# Revit family: 45-56-001-DN50-400
name_source: partatom
category: Pipe Accessories
units: mm (PartAtom-declared; Revit-internal decimal feet)

## family parameters
Always vertical = No
Cut with Voids When Loaded = No
Part Type = Valve - Breaks Into
Round Connector Dimension = Use Diameter
Shared = No
Work Plane-Based = No

## types (11) — shared parameters
Body_Wallthickness = 15 mm  [stored 0.0492126 ft]
DN 050 = Yes
DN 065 = Yes
DN 080 = Yes
DN 100 = Yes
DN 150 = Yes
DN 200 = Yes
DN 250 = Yes
DN 300 = Yes
DN 350 = Yes
DN 400 = Yes
DN050_PN10/16 = 45-050-56-01614020
DN065_PN10/16 = 45-065-56-01614020
DN080_PN10/16 = 45-080-56-01614020
DN100_PN10/16 = 45-100-56-01614020
DN150_PN10/16 = 45-150-56-01614020
DN200_PN10 = 45-200-56-00614020
DN200_PN16 = 45-200-56-01614020
DN250_PN10 = 45-250-56-006B4020
DN250_PN16 = 45-250-56-016B4020
DN300_PN10 = 45-300-5C-006B4020
DN300_PN16 = 45-300-5C-016B4020
DN350_PN10 = 45-350-5C-01614020
DN350_PN16 = 45-350-5C-016B4020
DN400_PN10 = 45-400-5C-006B4020
DN400_PN16 = 45-400-5C-01614020
DN400_PN16(2) = 45-400-5C-016B4020
Description_ = AVK GATE VALVE, AWWA, FLANGED
Ftc = 4 mm  [stored 0.0131234 ft]
Name_Height_reference = 10 mm  [stored 0.0328084 ft]
Rib_Thickness = 18 mm  [stored 0.0590551 ft]
Search_table = 45-56-001-DN50-400
URL product pages = https://www.avkvalves.com
zero-valued in all types: Bottom_Reference

## per-type parameters (varying)
- DN 065: At=64 mm; Body_Height=128 mm; Body_depth=128 mm; Body_width=60 mm; Bonnet_Flange_Depth=150 mm; Bonnet_Flange_Width=65 mm; Bonnet_Flange_cut=7.5 mm  [stored 0.0246063 ft]; Bonnet_Flange_thickness=15 mm  [stored 0.0492126 ft]; Bonnet_H=145 mm; Bonnet_H_Ref=197 mm; Bonnet_Height=44.5 mm; Bonnet_Reference_height=118 mm; Bonnet_Thickness=61.2 mm; Bonnet_W=60 mm; Bt=61.2 mm; Bt_2=54 mm; CL _Thickness=19 mm  [stored 0.062336 ft]; CL_Height=69 mm; CL_Height_2=23 mm  [stored 0.0754593 ft]; Cut_Reference=380 mm; D=82.5 mm; D1=10 mm  [stored 0.0328084 ft]; Fillet_Thickness=6 mm  [stored 0.019685 ft]; Flange_OR=89 mm; Flange_Thickness=19 mm  [stored 0.062336 ft]; Flange_Thickness_cut=28.25 mm  [stored 0.0926837 ft]; Ftc_reference_height=89 mm; HW_Dia=15 mm  [stored 0.0492126 ft]; HW_H_ref=7.5 mm  [stored 0.0246063 ft]; HW_Rib_depth=152 mm; HW_Rib_width=15 mm  [stored 0.0492126 ft]; Hc=380 mm; Ho=450 mm; ID (Radius)=32.5 mm  [stored 0.106627 ft]; L=190 mm; L_Dia=65 mm; Name_Reference=96 mm; Name_Width=30 mm  [stored 0.0984252 ft]; Neck_T=17 mm  [stored 0.0557743 ft]; Nominal Diameter (DN)=65 mm; R1tv=890 mm; R2f=15 mm  [stored 0.0492126 ft]; Rib_Height_Reference_1=120 mm; Rib_Height_Reference_2=110 mm; Rib_Height_Reference_3=100 mm; Rib_Height_Reference_4=75 mm; Rib_Width_1=30 mm  [stored 0.0984252 ft]; Rib_Width_2=30 mm  [stored 0.0984252 ft]; Rib_Width_3=30 mm  [stored 0.0984252 ft]; Rib_depth_1=30 mm  [stored 0.0984252 ft]; Rib_depth_2=30 mm  [stored 0.0984252 ft]; Rib_depth_3=30 mm  [stored 0.0984252 ft]; Rt=296.67 mm; W1=82.5 mm; W2=178 mm
- DN 080: At=64 mm; Body_Height=135 mm; Body_depth=128 mm; Body_width=75 mm; Bonnet_Flange_Depth=150 mm; Bonnet_Flange_Width=96 mm; Bonnet_Flange_cut=7.5 mm  [stored 0.0246063 ft]; Bonnet_Flange_thickness=15 mm  [stored 0.0492126 ft]; Bonnet_H=153 mm; Bonnet_H_Ref=204 mm; Bonnet_Height=47.75 mm; Bonnet_Reference_height=125 mm; Bonnet_Thickness=76.5 mm; Bonnet_W=70 mm; Bt=76.5 mm; Bt_2=69 mm; CL _Thickness=26.5 mm  [stored 0.0869423 ft]; CL_Height=69 mm; CL_Height_2=23 mm  [stored 0.0754593 ft]; Cut_Reference=406 mm; D=82.5 mm; D1=10 mm  [stored 0.0328084 ft]; Fillet_Thickness=6 mm  [stored 0.019685 ft]; Flange_OR=95.5 mm; Flange_Thickness=19 mm  [stored 0.062336 ft]; Flange_Thickness_cut=27.75 mm  [stored 0.0910433 ft]; Ftc_reference_height=95.5 mm; HW_Dia=15 mm  [stored 0.0492126 ft]; HW_H_ref=7.5 mm  [stored 0.0246063 ft]; HW_Rib_depth=152 mm; HW_Rib_width=15 mm  [stored 0.0492126 ft]; Hc=395 mm; Ho=478 mm; ID (Radius)=40 mm; L=203 mm; L_Dia=80 mm; Name_Reference=90 mm; Name_Width=37.5 mm; Neck_T=24.5 mm  [stored 0.0803806 ft]; Nominal Diameter (DN)=80 mm; R1tv=955 mm; R2f=15 mm  [stored 0.0492126 ft]; Rib_Height_Reference_1=120 mm; Rib_Height_Reference_2=110 mm; Rib_Height_Reference_3=100 mm; Rib_Height_Reference_4=85 mm; Rib_Width_1=37.5 mm; Rib_Width_2=37.5 mm; Rib_Width_3=37.5 mm; Rib_depth_1=37.5 mm; Rib_depth_2=37.5 mm; Rib_depth_3=37.5 mm; Rt=318.33 mm; W1=82.5 mm; W2=191 mm
- DN 100: At=80 mm; Body_Height=149 mm; Body_depth=160 mm; Body_width=80 mm; Bonnet_Flange_Depth=180 mm; Bonnet_Flange_Width=81 mm; Bonnet_Flange_cut=7.5 mm  [stored 0.0246063 ft]; Bonnet_Flange_thickness=15 mm  [stored 0.0492126 ft]; Bonnet_H=195.67 mm; Bonnet_H_Ref=234 mm; Bonnet_Height=57.25 mm; Bonnet_Reference_height=139 mm; Bonnet_Thickness=81.6 mm; Bonnet_W=80 mm; Bt=81.6 mm; Bt_2=74 mm; CL _Thickness=29 mm  [stored 0.0951444 ft]; CL_Height=85 mm; CL_Height_2=28.33 mm; Cut_Reference=458 mm; D=69.5 mm; D1=12.5 mm  [stored 0.0410105 ft]; Fillet_Thickness=6 mm  [stored 0.019685 ft]; Flange_OR=114.5 mm; Flange_Thickness=19 mm  [stored 0.062336 ft]; Flange_Thickness_cut=32.25 mm; Ftc_reference_height=114.5 mm; HW_Dia=15 mm  [stored 0.0492126 ft]; HW_H_ref=7.5 mm  [stored 0.0246063 ft]; HW_Rib_depth=126 mm; HW_Rib_width=15 mm  [stored 0.0492126 ft]; Hc=473 mm; Ho=575 mm; ID (Radius)=50 mm; L=229 mm; L_Dia=100 mm; Name_Reference=101 mm; Name_Width=40 mm; Neck_T=27 mm; Nominal Diameter (DN)=100 mm; R1tv=1145 mm; R2f=15 mm  [stored 0.0492126 ft]; Rib_Height_Reference_1=120 mm; Rib_Height_Reference_2=110 mm; Rib_Height_Reference_3=100 mm; Rib_Height_Reference_4=90 mm; Rib_Width_1=40 mm; Rib_Width_2=40 mm; Rib_Width_3=40 mm; Rib_depth_1=40 mm; Rib_depth_2=40 mm; Rib_depth_3=40 mm; Rt=381.67 mm; W1=119.5 mm; W2=229 mm
- DN 150: At=105.5 mm; Body_Height=206 mm; Body_depth=211 mm; Body_width=95 mm; Bonnet_Flange_Depth=250 mm; Bonnet_Flange_Width=154 mm; Bonnet_Flange_cut=7.5 mm  [stored 0.0246063 ft]; Bonnet_Flange_thickness=15 mm  [stored 0.0492126 ft]; Bonnet_H=266.67 mm; Bonnet_H_Ref=316.5 mm; Bonnet_Height=70 mm; Bonnet_Reference_height=196 mm; Bonnet_Thickness=96.9 mm; Bonnet_W=90 mm; Bt=96.9 mm; Bt_2=89 mm; CL _Thickness=33.5 mm; CL_Height=110.5 mm; CL_Height_2=36.83 mm; Cut_Reference=534 mm; D=145 mm; D1=14 mm  [stored 0.0459318 ft]; Fillet_Thickness=12 mm  [stored 0.0393701 ft]; Flange_OR=140 mm; Flange_Thickness=19 mm  [stored 0.062336 ft]; Flange_Thickness_cut=32.5 mm  [stored 0.106627 ft]; Ftc_reference_height=140 mm; HW_Dia=15 mm  [stored 0.0492126 ft]; HW_H_ref=7.5 mm  [stored 0.0246063 ft]; HW_Rib_depth=277 mm; HW_Rib_width=15 mm  [stored 0.0492126 ft]; Hc=635 mm; Ho=787 mm; ID (Radius)=75 mm; L=267 mm; L_Dia=150 mm; Name_Reference=143 mm; Name_Width=47.5 mm; Neck_T=31.5 mm  [stored 0.103346 ft]; Nominal Diameter (DN)=150 mm; R1tv=1400 mm; R2f=30 mm  [stored 0.0984252 ft]; Rib_Height_Reference_1=120 mm; Rib_Height_Reference_2=110 mm; Rib_Height_Reference_3=100 mm; Rib_Height_Reference_4=100 mm; Rib_Width_1=50 mm; Rib_Width_2=47.5 mm; Rib_Width_3=47.5 mm; Rib_depth_1=50 mm; Rib_depth_2=47.5 mm; Rib_depth_3=47.5 mm; Rt=466.67 mm; W1=145 mm; W2=280 mm
- DN 200: At=131.5 mm; Body_Height=290 mm; Body_depth=263 mm; Body_width=108 mm; Bonnet_Flange_Depth=283 mm; Bonnet_Flange_Width=154 mm; Bonnet_Flange_cut=12.5 mm  [stored 0.0410105 ft]; Bonnet_Flange_thickness=25 mm  [stored 0.082021 ft]; Bonnet_H=295 mm; Bonnet_H_Ref=426.5 mm; Bonnet_Height=85.75 mm; Bonnet_Reference_height=280 mm; Bonnet_Thickness=110.16 mm; Bonnet_W=100 mm; Bt=110.16 mm; Bt_2=102 mm; CL _Thickness=34 mm  [stored 0.111549 ft]; CL_Height=136.5 mm; CL_Height_2=45.5 mm; Cut_Reference=584 mm; D=168 mm; D1=16 mm  [stored 0.0524934 ft]; Fillet_Thickness=24 mm  [stored 0.0787402 ft]; Flange_OR=171.5 mm; Flange_Thickness=20 mm  [stored 0.0656168 ft]; Flange_Thickness_cut=35.75 mm; Ftc_reference_height=171.5 mm; HW_Dia=20 mm  [stored 0.0656168 ft]; HW_H_ref=10 mm  [stored 0.0328084 ft]; HW_Rib_depth=318 mm; HW_Rib_width=20 mm  [stored 0.0656168 ft]; Hc=787 mm; Ho=991 mm; ID (Radius)=100 mm; L=292 mm; L_Dia=200 mm; Name_Reference=183 mm; Name_Width=54 mm; Neck_T=32 mm  [stored 0.104987 ft]; Nominal Diameter (DN)=200 mm; R1tv=1715 mm; R2f=60 mm; Rib_Height_Reference_1=120 mm; Rib_Height_Reference_2=110 mm; Rib_Height_Reference_3=100 mm; Rib_Height_Reference_4=180 mm; Rib_Width_1=128 mm; Rib_Width_2=128 mm; Rib_Width_3=54 mm; Rib_depth_1=303 mm; Rib_depth_2=303 mm; Rib_depth_3=54 mm; Rt=571.67 mm; W1=168 mm; W2=343 mm
- DN 050: At=57.5 mm; Body_Height=115 mm; Body_depth=115 mm; Body_width=55 mm; Bonnet_Flange_Depth=140 mm; Bonnet_Flange_Width=55 mm; Bonnet_Flange_cut=7.5 mm  [stored 0.0246063 ft]; Bonnet_Flange_thickness=15 mm  [stored 0.0492126 ft]; Bonnet_H=186.67 mm; Bonnet_H_Ref=177.5 mm; Bonnet_Height=41.25 mm; Bonnet_Reference_height=105 mm; Bonnet_Thickness=56.1 mm; Bonnet_W=50 mm; Bt=56.1 mm; Bt_2=49 mm; CL _Thickness=16.5 mm  [stored 0.0541339 ft]; CL_Height=62.5 mm; CL_Height_2=20.83 mm; Cut_Reference=338 mm; D=82.5 mm; D1=10 mm  [stored 0.0328084 ft]; Fillet_Thickness=6 mm  [stored 0.019685 ft]; Flange_OR=82.5 mm; Flange_Thickness=19 mm  [stored 0.062336 ft]; Flange_Thickness_cut=28.75 mm; Ftc_reference_height=82.5 mm; HW_Dia=15 mm  [stored 0.0492126 ft]; HW_H_ref=7.5 mm  [stored 0.0246063 ft]; HW_Rib_depth=152 mm; HW_Rib_width=15 mm  [stored 0.0492126 ft]; Hc=400 mm; Ho=450 mm; ID (Radius)=25 mm  [stored 0.082021 ft]; L=169 mm; L_Dia=50 mm; Name_Reference=71 mm; Name_Width=27.5 mm  [stored 0.0902231 ft]; Neck_T=14.5 mm  [stored 0.0475722 ft]; Nominal Diameter (DN)=50 mm; R1tv=825 mm; R2f=15 mm  [stored 0.0492126 ft]; Rib_Height_Reference_1=120 mm; Rib_Height_Reference_2=110 mm; Rib_Height_Reference_3=100 mm; Rib_Height_Reference_4=75 mm; Rib_Width_1=27.5 mm  [stored 0.0902231 ft]; Rib_Width_2=27.5 mm  [stored 0.0902231 ft]; Rib_Width_3=27.5 mm  [stored 0.0902231 ft]; Rib_depth_1=27.5 mm  [stored 0.0902231 ft]; Rib_depth_2=27.5 mm  [stored 0.0902231 ft]; Rib_depth_3=27.5 mm  [stored 0.0902231 ft]; Rt=275 mm; W1=82.5 mm; W2=165 mm
- DN 250: At=173.5 mm; Body_Height=307 mm; Body_depth=347 mm; Body_width=150 mm; Bonnet_Flange_Depth=404 mm; Bonnet_Flange_Width=200 mm; Bonnet_Flange_cut=12.5 mm  [stored 0.0410105 ft]; Bonnet_Flange_thickness=25 mm  [stored 0.082021 ft]; Bonnet_H=370 mm; Bonnet_H_Ref=485.5 mm; Bonnet_Height=101.5 mm; Bonnet_Reference_height=297 mm; Bonnet_Thickness=153 mm; Bonnet_W=110 mm; Bt=153 mm; Bt_2=144 mm; CL _Thickness=55 mm; CL_Height=178.5 mm; CL_Height_2=59.5 mm; Cut_Reference=660 mm; D=206 mm; D1=16 mm  [stored 0.0524934 ft]; Fillet_Thickness=24 mm  [stored 0.0787402 ft]; Flange_OR=203 mm; Flange_Thickness=22 mm  [stored 0.0721785 ft]; Flange_Thickness_cut=39 mm; Ftc_reference_height=203 mm; HW_Dia=20 mm  [stored 0.0656168 ft]; HW_H_ref=10 mm  [stored 0.0328084 ft]; HW_Rib_depth=394 mm; HW_Rib_width=20 mm  [stored 0.0656168 ft]; Hc=935 mm; Ho=1189 mm; ID (Radius)=125 mm; L=330 mm; L_Dia=250 mm; Name_Reference=270 mm; Name_Width=75 mm; Neck_T=53 mm; Nominal Diameter (DN)=250 mm; R1tv=2030 mm; R2f=60 mm; Rib_Height_Reference_1=90 mm; Rib_Height_Reference_2=110 mm; Rib_Height_Reference_3=100 mm; Rib_Height_Reference_4=200 mm; Rib_Width_1=195 mm; Rib_Width_2=195 mm; Rib_Width_3=75 mm; Rib_depth_1=436 mm; Rib_depth_2=436 mm; Rib_depth_3=75 mm; Rt=676.67 mm; W1=206 mm; W2=406 mm
- DN 300: At=213 mm; Body_Height=372 mm; Body_depth=426 mm; Body_width=190 mm; Bonnet_Flange_Depth=483 mm; Bonnet_Flange_Width=240 mm; Bonnet_Flange_cut=17.5 mm  [stored 0.0574147 ft]; Bonnet_Flange_thickness=35 mm  [stored 0.114829 ft]; Bonnet_H=366.33 mm; Bonnet_H_Ref=590 mm; Bonnet_Height=120.75 mm; Bonnet_Reference_height=362 mm; Bonnet_Thickness=193.8 mm; Bonnet_W=120 mm; Bt=193.8 mm; Bt_2=184 mm; CL _Thickness=75 mm; CL_Height=218 mm; CL_Height_2=72.67 mm; Cut_Reference=712 mm; D=203.5 mm; D1=16 mm  [stored 0.0524934 ft]; Fillet_Thickness=24 mm  [stored 0.0787402 ft]; Flange_OR=241.5 mm; Flange_Thickness=24.5 mm  [stored 0.0803806 ft]; Flange_Thickness_cut=45.75 mm; Ftc_reference_height=241.5 mm; HW_Dia=25 mm  [stored 0.082021 ft]; HW_H_ref=12.5 mm  [stored 0.0410105 ft]; HW_Rib_depth=384 mm; HW_Rib_width=25 mm  [stored 0.082021 ft]; Hc=1054 mm; Ho=1359 mm; ID (Radius)=150 mm; L=356 mm; L_Dia=300 mm; Name_Reference=250 mm; Name_Width=95 mm; Neck_T=73 mm; Nominal Diameter (DN)=300 mm; R1tv=2415 mm; R2f=60 mm; Rib_Height_Reference_1=178 mm; Rib_Height_Reference_2=285 mm; Rib_Height_Reference_3=150 mm; Rib_Height_Reference_4=300 mm; Rib_Width_1=248 mm; Rib_Width_2=248 mm; Rib_Width_3=95 mm; Rib_depth_1=521 mm; Rib_depth_2=521 mm; Rib_depth_3=95 mm; Rt=805 mm; W1=203.5 mm; W2=483 mm
- DN 350: At=267 mm; Body_Height=508 mm; Body_depth=534 mm; Body_width=180 mm; Bonnet_Flange_Depth=586 mm; Bonnet_Flange_Width=250 mm; Bonnet_Flange_cut=17.5 mm  [stored 0.0574147 ft]; Bonnet_Flange_thickness=35 mm  [stored 0.114829 ft]; Bonnet_H=488.33 mm; Bonnet_H_Ref=780 mm; Bonnet_Height=133.25 mm; Bonnet_Reference_height=498 mm; Bonnet_Thickness=183.6 mm; Bonnet_W=130 mm; Bt=183.6 mm; Bt_2=174 mm; CL _Thickness=70 mm; CL_Height=272 mm; CL_Height_2=90.67 mm; Cut_Reference=762 mm; D=307.5 mm; D1=18 mm  [stored 0.0590551 ft]; Fillet_Thickness=24 mm  [stored 0.0787402 ft]; Flange_OR=266.5 mm; Flange_Thickness=26.5 mm  [stored 0.0869423 ft]; Flange_Thickness_cut=45.75 mm; Ftc_reference_height=266.5 mm; HW_Dia=25 mm  [stored 0.082021 ft]; HW_H_ref=12.5 mm  [stored 0.0410105 ft]; HW_Rib_depth=592 mm; HW_Rib_width=25 mm  [stored 0.082021 ft]; Hc=1384 mm; Ho=1795 mm; ID (Radius)=175 mm; L=381 mm; L_Dia=350 mm; Name_Reference=404 mm; Name_Width=90 mm; Neck_T=68 mm; Nominal Diameter (DN)=350 mm; R1tv=2665 mm; R2f=60 mm; Rib_Height_Reference_1=70 mm; Rib_Height_Reference_2=185 mm; Rib_Height_Reference_3=305 mm; Rib_Height_Reference_4=410 mm; Rib_Width_1=292 mm; Rib_Width_2=292 mm; Rib_Width_3=292 mm; Rib_depth_1=586 mm; Rib_depth_2=586 mm; Rib_depth_3=586 mm; Rt=888.33 mm; W1=307.5 mm; W2=533 mm
- DN 400_ PN10/16: At=267 mm; Body_Height=508 mm; Body_depth=534 mm; Body_width=200 mm; Bonnet_Flange_Depth=586 mm; Bonnet_Flange_Width=300 mm; Bonnet_Flange_cut=35 mm  [stored 0.114829 ft]; Bonnet_Flange_thickness=70 mm; Bonnet_H=484.33 mm; Bonnet_H_Ref=780 mm; Bonnet_Height=149.25 mm; Bonnet_Reference_height=498 mm; Bonnet_Thickness=204 mm; Bonnet_W=130 mm; Bt=204 mm; Bt_2=194 mm; CL _Thickness=76 mm; CL_Height=272 mm; CL_Height_2=90.67 mm; Cut_Reference=812 mm; D=305 mm; D1=18 mm  [stored 0.0590551 ft]; Fillet_Thickness=32 mm  [stored 0.104987 ft]; Flange_OR=298.5 mm; Flange_Thickness=28 mm  [stored 0.0918635 ft]; Flange_Thickness_cut=49.23 mm; Ftc_reference_height=298.5 mm; HW_Dia=30 mm  [stored 0.0984252 ft]; HW_H_ref=15 mm  [stored 0.0492126 ft]; HW_Rib_depth=582 mm; HW_Rib_width=30 mm  [stored 0.0984252 ft]; Hc=1385 mm; Ho=2113 mm; ID (Radius)=200.05 mm; L=406 mm; L_Dia=400.1 mm; Name_Reference=426 mm; Name_Width=100 mm; Neck_T=74 mm; Nominal Diameter (DN)=400.1 mm; R1tv=2985 mm; R2f=80 mm; Rib_Height_Reference_1=81 mm; Rib_Height_Reference_2=210 mm; Rib_Height_Reference_3=330 mm; Rib_Height_Reference_4=440 mm; Rib_Width_1=292 mm; Rib_Width_2=292 mm; Rib_Width_3=292 mm; Rib_depth_1=586 mm; Rib_depth_2=586 mm; Rib_depth_3=586 mm; Rt=995 mm; W1=305 mm; W2=597 mm
- DN 400_PN16: At=272 mm; Body_Height=523 mm; Body_depth=544 mm; Body_width=200 mm; Bonnet_Flange_Depth=586 mm; Bonnet_Flange_Width=300 mm; Bonnet_Flange_cut=35 mm  [stored 0.114829 ft]; Bonnet_Flange_thickness=70 mm; Bonnet_H=475.67 mm; Bonnet_H_Ref=800 mm; Bonnet_Height=149.25 mm; Bonnet_Reference_height=513 mm; Bonnet_Thickness=204 mm; Bonnet_W=140 mm; Bt=204 mm; Bt_2=194 mm; CL _Thickness=76 mm; CL_Height=277 mm; CL_Height_2=92.33 mm; Cut_Reference=812 mm; D=305 mm; D1=18 mm  [stored 0.0590551 ft]; Fillet_Thickness=32 mm  [stored 0.104987 ft]; Flange_OR=298.5 mm; Flange_Thickness=28 mm  [stored 0.0918635 ft]; Flange_Thickness_cut=49.21 mm; Ftc_reference_height=298.5 mm; HW_Dia=30 mm  [stored 0.0984252 ft]; HW_H_ref=15 mm  [stored 0.0492126 ft]; HW_Rib_depth=582 mm; HW_Rib_width=30 mm  [stored 0.0984252 ft]; Hc=1398 mm; Ho=1823 mm; ID (Radius)=200.08 mm; L=406 mm; L_Dia=400.16 mm; Name_Reference=426 mm; Name_Width=100 mm; Neck_T=74 mm; Nominal Diameter (DN)=400.16 mm; R1tv=2985 mm; R2f=80 mm; Rib_Height_Reference_1=81 mm; Rib_Height_Reference_2=210 mm; Rib_Height_Reference_3=330 mm; Rib_Height_Reference_4=440 mm; Rib_Width_1=292 mm; Rib_Width_2=292 mm; Rib_Width_3=292 mm; Rib_depth_1=586 mm; Rib_depth_2=586 mm; Rib_depth_3=586 mm; Rt=995 mm; W1=305 mm; W2=597 mm

note: [stored X ft] marks values corroborated as IEEE doubles in the binary element streams (Revit-internal decimal feet)

## geometry (parser evidence)
native form markers: Sweep x5
no freeform markers — native parametric forms only
